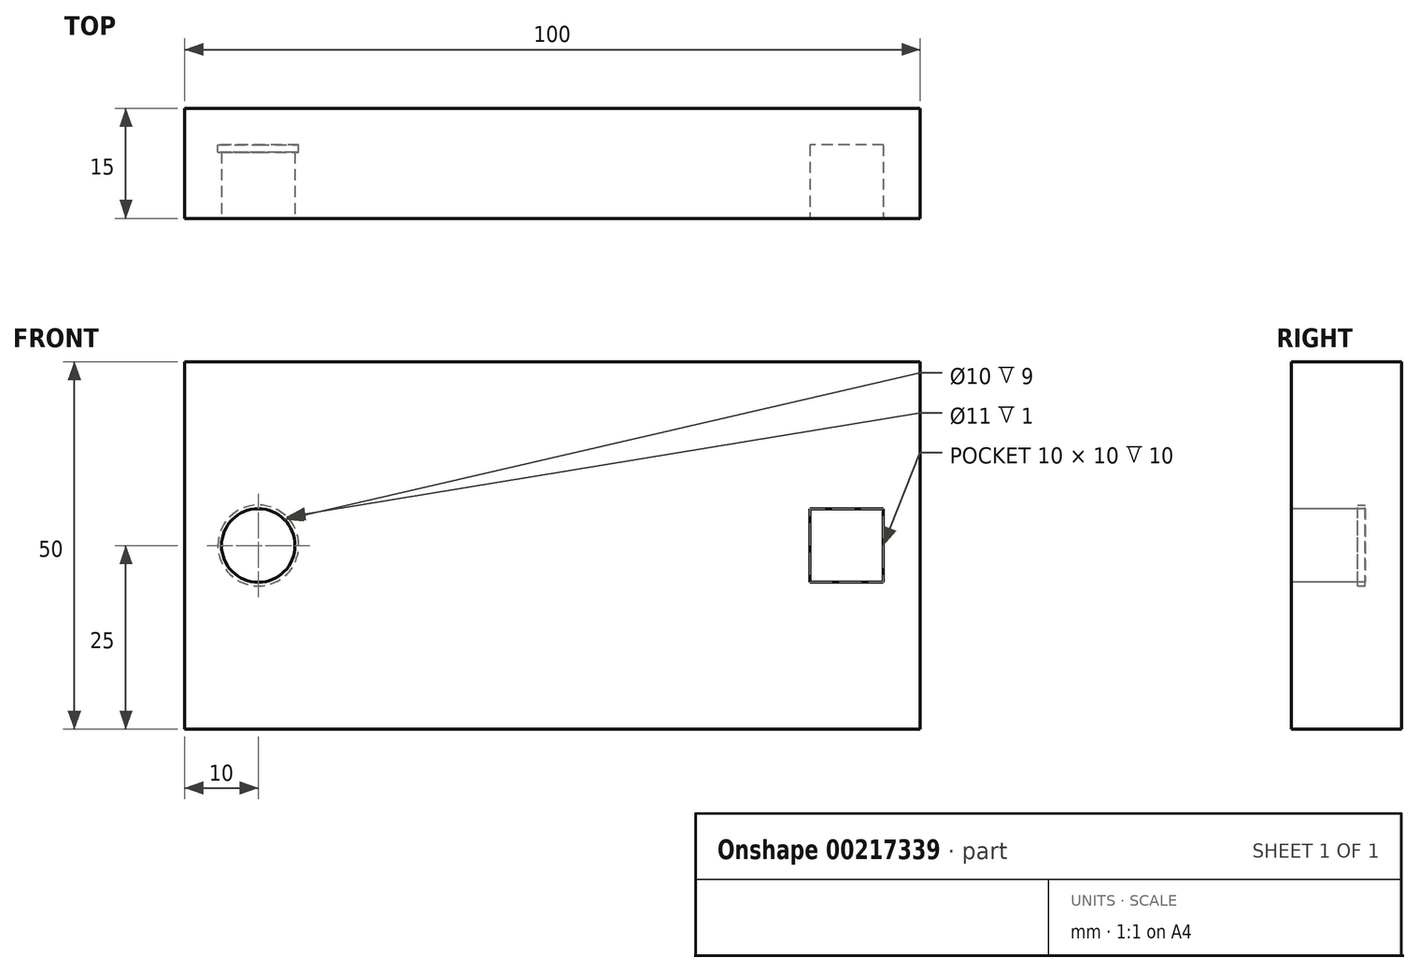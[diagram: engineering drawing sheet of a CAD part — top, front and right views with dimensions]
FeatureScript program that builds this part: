
annotation { "Feature Type Name" : "Feature", "Feature Type Description" : "" }
export const myFeature = defineFeature(function(context is Context, id is Id, definition is map)
    precondition{}
    {
        {
            var Q0;
            Q0=qCreatedBy(makeId("Front.planeOp"),FACE);
            var sketch = newSketch(context, id + "F0", { "sketchPlane" : qUnion([Q0])});
            skLineSegment(sketch, "E0.bottom", {"start": v(-50, 25) * mm, "end": v(50, 25) * mm});
            skLineSegment(sketch, "E0.top", {"start": v(-50, -25) * mm, "end": v(50, -25) * mm});
            skLineSegment(sketch, "E0.left", {"start": v(-50, 25) * mm, "end": v(-50, -25) * mm});
            skLineSegment(sketch, "E0.right", {"start": v(50, 25) * mm, "end": v(50, -25) * mm});
            skSolve(sketch);
        }
        {
            var Q0;
            Q0=makeQuery(id+"F0.imprint","IMPRINT",FACE,{"disambiguationData":[TD([[makeQuery(id+"F0.imprint","IMPRINT",EDGE,{"derivedFrom":sQuery(id+"F0.wireOp",EDGE,"E0.bottom")}),-1.0]])]});
            extrude(context, id + "F1", {"entities" : qUnion([Q0]), "endBound" : BoundingType.SYMMETRIC, "depth" : 15 * mm});
        }
        {
            var Q0;
            Q0=makeQuery(id+"F1.opExtrude","CAP_FACE",FACE,{"disambiguationData":[OSD([sQuery(id+"F0.wireOp",EDGE,"E0.bottom"),sQuery(id+"F0.wireOp",EDGE,"E0.top"),sQuery(id+"F0.wireOp",EDGE,"E0.left"),sQuery(id+"F0.wireOp",EDGE,"E0.right")])],"isStart":false});
            var sketch = newSketch(context, id + "F2", { "sketchPlane" : qUnion([Q0])});
            skCircle(sketch, "E1", {"center": v(-40, 0) * mm, "radius": 5 * mm});
            skLineSegment(sketch, "E2.bottom", {"start": v(45, 5) * mm, "end": v(35, 5) * mm});
            skLineSegment(sketch, "E2.top", {"start": v(45, -5) * mm, "end": v(35, -5) * mm});
            skLineSegment(sketch, "E2.left", {"start": v(45, 5) * mm, "end": v(45, -5) * mm});
            skLineSegment(sketch, "E2.right", {"start": v(35, 5) * mm, "end": v(35, -5) * mm});
            skPoint(sketch, "E2.middle", {"position": v(40, 0) * mm});
            skSolve(sketch);
        }
        {
            var Q0;
            Q0=makeQuery(id+"F2.imprint","IMPRINT",FACE,{"disambiguationData":[TD([[makeQuery(id+"F2.imprint","IMPRINT",EDGE,{"derivedFrom":sQuery(id+"F2.wireOp",EDGE,"E1")}),1.0]])]});
            var Q1;
            Q1=makeQuery(id+"F2.imprint","IMPRINT",FACE,{"disambiguationData":[TD([[makeQuery(id+"F2.imprint","IMPRINT",EDGE,{"derivedFrom":sQuery(id+"F2.wireOp",EDGE,"ISyAumyx-YnyH-t3wM-iWlK-nqlbmAxrx7Au")}),1.0]])]});
            var Q2;
            Q2=makeQuery(id+"F2.imprint","IMPRINT",FACE,{"disambiguationData":[TD([[makeQuery(id+"F2.imprint","IMPRINT",EDGE,{"derivedFrom":sQuery(id+"F2.wireOp",EDGE,"E2.bottom")}),1.0]])]});
            extrude(context, id + "F3", {"entities" : qUnion([Q0, Q1, Q2]), "operationType" : NewBodyOperationType.REMOVE, "oppositeDirection" : true, "depth" : 10 * mm});
        }
        {
            var Q0;
            Q0=makeQuery(id+"F3.boolean.opBoolean","COPY",FACE,{"derivedFrom":makeQuery(id+"F3.opExtrude","CAP_FACE",FACE,{"disambiguationData":[OSD([sQuery(id+"F2.wireOp",EDGE,"E1")])],"isStart":false})});
            var sketch = newSketch(context, id + "F4", { "sketchPlane" : qUnion([Q0])});
            skCircle(sketch, "E3", {"center": v(-40, 0) * mm, "radius": 5.5 * mm});
            skSolve(sketch);
        }
        {
            var Q0;
            Q0 = qSketchRegion(id + "F4", true);
            extrude(context, id + "F5", {"entities" : qUnion([Q0]), "operationType" : NewBodyOperationType.REMOVE, "depth" : 1 * mm});
        }
    });
